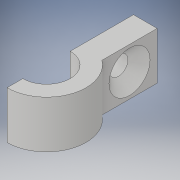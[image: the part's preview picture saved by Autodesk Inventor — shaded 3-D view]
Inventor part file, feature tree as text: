
AUTODESK INVENTOR PART (.ipt)
format: ipt  version: 2019 (Build 230136000, 136)  size: 120,832 bytes
history: native  units: mm
features: extrude x2, sketch x2, chamfer x1
ambient origin geometry x8: Origin, YZ Plane, XZ Plane, XY Plane, X Axis, Y Axis, Z Axis, Center Point
bodies: Solid1 (feature_tree)
feature tree (5):
  extrude  "Extrusion1"  Depth=1.5mm
  extrude  "Extrusion2"  Depth=3.0mm
  chamfer  "Chamfer1"  Distance=3.0mm
  sketch  "Sketch1"  dims[d0=1.5mm d1=1.0mm]
  sketch  "Sketch2"  dims[d2=1.5mm d3=3.0mm d4=3.0mm d5=0.0mm d6=1.2mm d7=3.0mm d8=0.0mm d9=0.7mm d10=2.0mm d11=45.0deg d12=14.3117mm d13=0.75mm d14=20.594885mm d15=0.0625mm d16=0.75mm d17=0.375mm]
